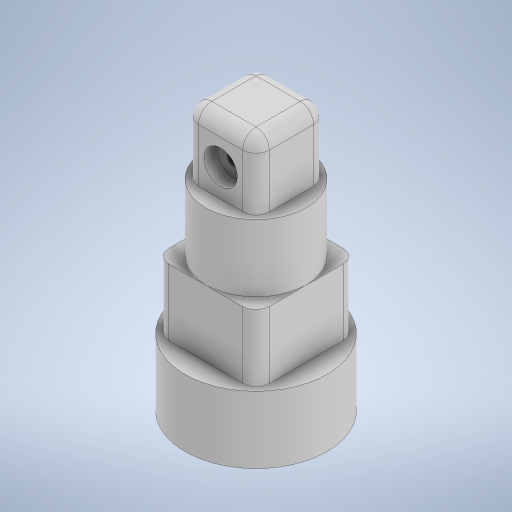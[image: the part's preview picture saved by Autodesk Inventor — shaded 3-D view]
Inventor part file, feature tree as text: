
AUTODESK INVENTOR PART (.ipt)
format: ipt  version: 2023 (Build 270158000, 158)  size: 354,816 bytes
history: native  units: mm
features: extrude x6, sketch x3, hole x3, fillet x1, shell x1, thread x1
ambient origin geometry x8: Origin, YZ Plane, XZ Plane, XY Plane, X Axis, Y Axis, Z Axis, Center Point
bodies: Solido1 (feature_tree)
feature tree (15):
  sketch  "Schizzo1"
  extrude  "Estrusione1"  Depth=15.0mm
  extrude  "Estrusione2"  Depth=40.0mm TaperAngle=0.0deg
  extrude  "Estrusione3"  Depth=30.0mm TaperAngle=0.0deg
  extrude  "Estrusione4"  Depth=30.0mm TaperAngle=0.0deg
  extrude  "Estrusione5"  Depth=20.0mm TaperAngle=0.0deg
  extrude  "Estrusione6"  Depth=20.0mm TaperAngle=0.0deg
  fillet  "Raccordo1"  Radius=10.0mm
  sketch  "Schizzo2"
  hole  "Foro1"  [1 undecoded]
  hole  "Foro2"  [1 undecoded]
  hole  "Foro3"  [1 undecoded]
  shell  "Svuotamento1"  [1 undecoded]
  thread  "Filettatura1"
  sketch  "Schizzo3"
note: 4 required parameter values undecoded (feature->parameter linkage not recoverable at this tier; creation-order binding heuristic only, values carry confidence <= 0.55)
